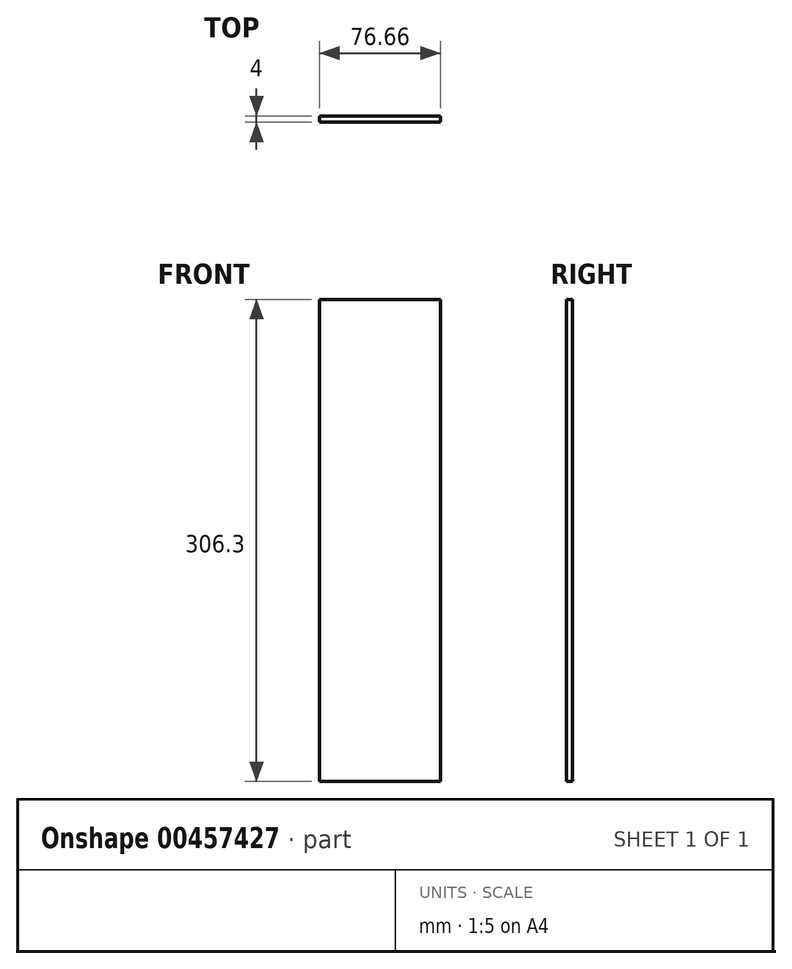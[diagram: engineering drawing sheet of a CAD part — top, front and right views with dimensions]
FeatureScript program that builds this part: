
annotation { "Feature Type Name" : "Feature", "Feature Type Description" : "" }
export const myFeature = defineFeature(function(context is Context, id is Id, definition is map)
    precondition{}
    {
        {
            var Q0;
            Q0=qCreatedBy(makeId("Front.planeOp"),FACE);
            var sketch = newSketch(context, id + "F0", { "sketchPlane" : qUnion([Q0])});
            skLineSegment(sketch, "E0.bottom", {"start": v(38.33, 153.15) * mm, "end": v(-38.33, 153.15) * mm});
            skLineSegment(sketch, "E0.top", {"start": v(38.33, -153.15) * mm, "end": v(-38.33, -153.15) * mm});
            skLineSegment(sketch, "E0.left", {"start": v(38.33, 153.15) * mm, "end": v(38.33, -153.15) * mm});
            skLineSegment(sketch, "E0.right", {"start": v(-38.33, 153.15) * mm, "end": v(-38.33, -153.15) * mm});
            skPoint(sketch, "E0.middle", {"position": v(0, 0) * mm});
            skSolve(sketch);
        }
        {
            var Q0;
            Q0=makeQuery(id+"F0.imprint","IMPRINT",FACE,{"disambiguationData":[TD([[makeQuery(id+"F0.imprint","IMPRINT",EDGE,{"derivedFrom":sQuery(id+"F0.wireOp",EDGE,"E0.bottom")}),1.0]])]});
            extrude(context, id + "F1", {"entities" : qUnion([Q0]), "depth" : 4 * mm});
        }
    });
